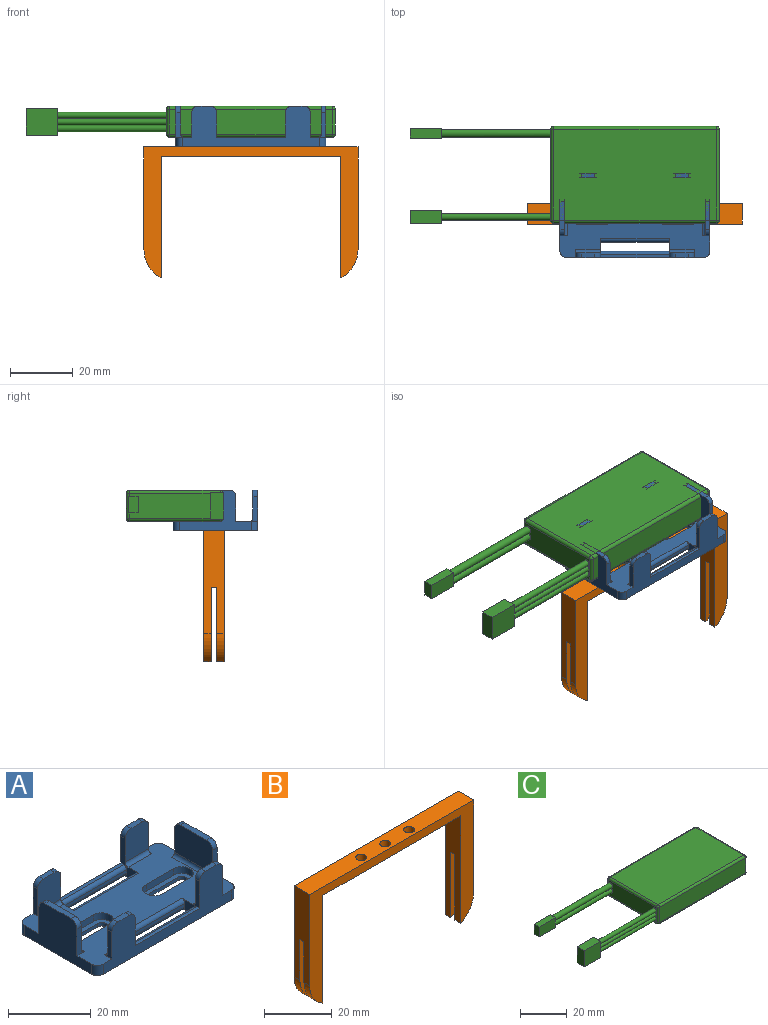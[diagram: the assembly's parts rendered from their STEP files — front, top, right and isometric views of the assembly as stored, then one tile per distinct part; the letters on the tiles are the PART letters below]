
ASSEMBLY  parts=3 mates=2
PART A: 88 faces, bbox 48x27x13 mm
  f0: plane 15x5.6mm, normal (0,0,1), area 42mm2, adj f66,f67,f68,f69,f74,f75,f76,f77
  f1: plane 48x27mm, normal (0,0,-1), area 1002mm2, adj f7,f8,f14,f15,f45,f47,f50,f52
  f2: plane 48x27mm, normal (0,0,1), area 729mm2, adj f7,f8,f14,f15,f21,f22,f23,f24
  f3: plane 22x1mm, normal (0,0,1), area 22mm2, adj f15,f25,f26,f60
  f4: plane 22x1mm, normal (0,0,1), area 22mm2, adj f14,f31,f32,f57
  f5: plane 9x8mm, normal (0,1,0), area 70.3mm2, adj f10,f29,f31,f33,f38,f86
  f6: plane 9x8mm, normal (0,-1,0), area 70.3mm2, adj f13,f26,f28,f36,f44,f84
  f7: plane 23x13mm, normal (1,0,0), area 197.3mm2, adj f1,f2,f9,f27,f30,f35,f37,f78
  f8: plane 23x13mm, normal (-1,0,0), area 197.3mm2, adj f1,f2,f11,f21,f24,f39,f41,f80
  f9: plane 9x1.5mm, normal (0,0,1), area 13.5mm2, adj f7,f17,f35,f37
  f10: plane 4x1.5mm, normal (0,0,1), area 6mm2, adj f5,f14,f33,f38
  f11: plane 9x1.5mm, normal (0,0,1), area 13.5mm2, adj f8,f19,f39,f41
  f12: plane 4x1.5mm, normal (0,0,1), area 6mm2, adj f15,f18,f42,f43
  f13: plane 4x1.5mm, normal (0,0,1), area 6mm2, adj f6,f15,f36,f44
  f14: plane 44x13mm, normal (0,-1,0), area 288.6mm2, adj f1,f2,f4,f10,f20,f23,f29,f31
  f15: plane 44x13mm, normal (0,1,0), area 288.6mm2, adj f1,f2,f3,f12,f13,f22,f25,f26
  f16: plane 9x8mm, normal (0,1,0), area 70.3mm2, adj f20,f23,f32,f34,f40,f83
  f17: plane 13x9mm, normal (-1,0,0), area 115.3mm2, adj f9,f27,f30,f35,f37,f85
  f18: plane 9x8mm, normal (0,-1,0), area 70.3mm2, adj f12,f22,f25,f42,f43,f82
  f19: plane 13x9mm, normal (1,0,0), area 115.3mm2, adj f11,f21,f24,f39,f41,f87
  f20: plane 4x1.5mm, normal (0,0,1), area 6mm2, adj f14,f16,f34,f40
  f21: plane 8x2.5mm, normal (0,1,0), area 12.2mm2, adj f2,f8,f19,f41,f87
  f22: plane 8x2.5mm, normal (-1,0,0), area 12.2mm2, adj f2,f15,f18,f42,f82
  f23: plane 8x2.5mm, normal (-1,0,0), area 12.2mm2, adj f2,f14,f16,f40,f83
  f24: plane 8x2.5mm, normal (0,-1,0), area 12.2mm2, adj f2,f8,f19,f39,f87
  f25: plane 8x2.5mm, normal (1,0,0), area 12.2mm2, adj f3,f15,f18,f43,f50,f82
  f26: plane 8x2.5mm, normal (-1,0,0), area 12.2mm2, adj f3,f6,f15,f44,f52,f84
  f27: plane 8x2.5mm, normal (0,1,0), area 12.2mm2, adj f2,f7,f17,f35,f85
  f28: plane 8x2.5mm, normal (1,0,0), area 12.2mm2, adj f2,f6,f15,f36,f84
  f29: plane 8x2.5mm, normal (1,0,0), area 12.2mm2, adj f2,f5,f14,f38,f86
  f30: plane 8x2.5mm, normal (0,-1,0), area 12.2mm2, adj f2,f7,f17,f37,f85
  f31: plane 8x2.5mm, normal (-1,0,0), area 12.2mm2, adj f4,f5,f14,f33,f47,f86
  f32: plane 8x2.5mm, normal (1,0,0), area 12.2mm2, adj f4,f14,f16,f34,f45,f83
  f33: cylinder r=2mm len=2mm, axis (0,-1,0), area 4.7mm2, adj f5,f10,f14,f31
  f34: cylinder r=2mm len=2mm, axis (0,1,0), area 4.7mm2, adj f14,f16,f20,f32
  f35: cylinder r=2mm len=2mm, axis (-1,0,0), area 4.7mm2, adj f7,f9,f17,f27
  f36: cylinder r=2mm len=2mm, axis (0,1,0), area 4.7mm2, adj f6,f13,f15,f28
  f37: cylinder r=2mm len=2mm, axis (1,0,0), area 4.7mm2, adj f7,f9,f17,f30
  f38: cylinder r=2mm len=2mm, axis (0,1,0), area 4.7mm2, adj f5,f10,f14,f29
  f39: cylinder r=2mm len=2mm, axis (1,0,0), area 4.7mm2, adj f8,f11,f19,f24
  f40: cylinder r=2mm len=2mm, axis (0,-1,0), area 4.7mm2, adj f14,f16,f20,f23
  f41: cylinder r=2mm len=2mm, axis (-1,0,0), area 4.7mm2, adj f8,f11,f19,f21
  f42: cylinder r=2mm len=2mm, axis (0,-1,0), area 4.7mm2, adj f12,f15,f18,f22
  f43: cylinder r=2mm len=2mm, axis (0,1,0), area 4.7mm2, adj f12,f15,f18,f25
  f44: cylinder r=2mm len=2mm, axis (0,-1,0), area 4.7mm2, adj f6,f13,f15,f26
  f45: plane 5x3mm, normal (1,0,0), area 9.9mm2, adj f1,f2,f32,f46,f48,f55,f56,f57
  f46: plane 22x1mm, normal (0,1,0), area 22mm2, adj f45,f47,f55,f57
  f47: plane 5x3mm, normal (-1,0,0), area 9.9mm2, adj f1,f2,f31,f46,f48,f55,f56,f57
  f48: plane 22x1mm, normal (0,-1,0), area 22mm2, adj f45,f47,f56,f58
  f49: plane 22x1mm, normal (0,-1,0), area 22mm2, adj f50,f52,f53,f60
  f50: plane 5x3mm, normal (1,0,0), area 9.9mm2, adj f1,f2,f25,f49,f51,f53,f54,f59
  f51: plane 22x1mm, normal (0,1,0), area 22mm2, adj f50,f52,f54,f59
  f52: plane 5x3mm, normal (-1,0,0), area 9.9mm2, adj f1,f2,f26,f49,f51,f53,f54,f59
  f53: cylinder r=1mm len=22mm, axis (-1,0,0), area 34.6mm2, adj f1,f49,f50,f52
  f54: cylinder r=1mm len=22mm, axis (1,0,0), area 34.6mm2, adj f1,f50,f51,f52
  f55: cylinder r=1mm len=22mm, axis (1,0,0), area 34.6mm2, adj f1,f45,f46,f47
  f56: cylinder r=1mm len=22mm, axis (-1,0,0), area 34.6mm2, adj f1,f45,f47,f48
  f57: cylinder r=1mm len=22mm, axis (-1,0,0), area 34.6mm2, adj f4,f45,f46,f47
  f58: cylinder r=1mm len=22mm, axis (1,0,0), area 34.6mm2, adj f2,f45,f47,f48
  f59: cylinder r=1mm len=22mm, axis (-1,0,0), area 34.6mm2, adj f2,f50,f51,f52
  f60: cylinder r=1mm len=22mm, axis (1,0,0), area 34.6mm2, adj f3,f49,f50,f52
  f61: cylinder r=2.8mm len=5.6mm, axis (0,0,1), area 17.6mm2, adj f2,f62,f64,f65
  f62: plane 9.4x2mm, normal (0,1,0), area 18.8mm2, adj f2,f61,f63,f65
  f63: cylinder r=2.8mm len=5.6mm, axis (0,0,1), area 17.6mm2, adj f2,f62,f64,f65
  f64: plane 9.4x2mm, normal (0,-1,0), area 18.8mm2, adj f2,f61,f63,f65
  f65: plane 15x5.6mm, normal (0,0,1), area 42mm2, adj f61,f62,f63,f64,f70,f71,f72,f73
  f66: cylinder r=2.8mm len=5.6mm, axis (0,0,1), area 17.6mm2, adj f0,f2,f67,f69
  f67: plane 9.4x2mm, normal (0,-1,0), area 18.8mm2, adj f0,f2,f66,f68
  f68: cylinder r=2.8mm len=5.6mm, axis (0,0,1), area 17.6mm2, adj f0,f2,f67,f69
  f69: plane 9.4x2mm, normal (0,1,0), area 18.8mm2, adj f0,f2,f66,f68
  f70: cylinder r=1.5mm len=3mm, axis (0,0,1), area 4.7mm2, adj f1,f65,f71,f73
  f71: plane 9.4x1mm, normal (0,1,0), area 9.4mm2, adj f1,f65,f70,f72
  f72: cylinder r=1.5mm len=3mm, axis (0,0,1), area 4.7mm2, adj f1,f65,f71,f73
  f73: plane 9.4x1mm, normal (0,-1,0), area 9.4mm2, adj f1,f65,f70,f72
  f74: cylinder r=1.5mm len=3mm, axis (0,0,1), area 4.7mm2, adj f0,f1,f75,f77
  f75: plane 9.4x1mm, normal (0,-1,0), area 9.4mm2, adj f0,f1,f74,f76
  f76: cylinder r=1.5mm len=3mm, axis (0,0,1), area 4.7mm2, adj f0,f1,f75,f77
  f77: plane 9.4x1mm, normal (0,1,0), area 9.4mm2, adj f0,f1,f74,f76
  f78: cylinder r=2mm len=3mm, axis (0,0,1), area 9.4mm2, adj f1,f2,f7,f14
  f79: cylinder r=2mm len=3mm, axis (0,0,-1), area 9.4mm2, adj f1,f2,f7,f15
  f80: cylinder r=2mm len=3mm, axis (0,0,1), area 9.4mm2, adj f1,f2,f8,f15
  f81: cylinder r=2mm len=3mm, axis (0,0,-1), area 9.4mm2, adj f1,f2,f8,f14
  f82: cylinder r=1mm len=8mm, axis (1,0,0), area 12.6mm2, adj f2,f18,f22,f25
  f83: cylinder r=1mm len=8mm, axis (-1,0,0), area 12.6mm2, adj f2,f16,f23,f32
  f84: cylinder r=1mm len=8mm, axis (1,0,0), area 12.6mm2, adj f2,f6,f26,f28
  f85: cylinder r=1mm len=13mm, axis (0,-1,0), area 20.4mm2, adj f2,f17,f27,f30
  f86: cylinder r=1mm len=8mm, axis (-1,0,0), area 12.6mm2, adj f2,f5,f29,f31
  f87: cylinder r=1mm len=13mm, axis (0,1,0), area 20.4mm2, adj f2,f19,f21,f24
PART B: 21 faces, bbox 68.5x6.5x41.9 mm
  f0: cylinder r=1.6mm len=3.2mm, axis (0,0,-1), area 30.2mm2, adj f15,f16
  f1: cylinder r=1.6mm len=3.2mm, axis (0,0,-1), area 30.2mm2, adj f15,f16
  f2: plane 38.87x6.5mm, normal (-1,0,0), area 212.4mm2, adj f4,f6,f7,f10,f12,f16,f18,f19
  f3: plane 32.94x6.5mm, normal (1,0,0), area 189mm2, adj f4,f6,f7,f10,f12,f15,f18,f19
  f4: cylinder r=10mm len=8.93mm, axis (0,-1,0), area 26.5mm2, adj f2,f3,f6,f12
  f5: cylinder r=10mm len=8.93mm, axis (0,-1,0), area 26.5mm2, adj f6,f9,f13,f20
  f6: plane 68.5x41.87mm, normal (0,-1,0), area 605.1mm2, adj f2,f3,f4,f5,f9,f15,f16,f20
  f7: cylinder r=10mm len=8.93mm, axis (0,-1,0), area 26.5mm2, adj f2,f3,f18,f19
  f8: cylinder r=10mm len=8.93mm, axis (0,-1,0), area 26.5mm2, adj f9,f14,f19,f20
  f9: plane 38.87x6.5mm, normal (1,0,0), area 212.4mm2, adj f5,f6,f8,f11,f13,f14,f16,f19
  f10: plane 5.5x1.7mm, normal (0,0,-1), area 9.3mm2, adj f2,f3,f12,f18
  f11: plane 5.5x1.7mm, normal (0,0,-1), area 9.4mm2, adj f9,f13,f14,f20
  f12: plane 23.71x5.5mm, normal (0,1,0), area 116.4mm2, adj f2,f3,f4,f10
  f13: plane 23.71x5.5mm, normal (0,1,0), area 116.4mm2, adj f5,f9,f11,f20
  f14: plane 23.71x5.5mm, normal (0,-1,0), area 116.4mm2, adj f8,f9,f11,f20
  f15: plane 68.5x6.5mm, normal (0,0,1), area 421.1mm2, adj f0,f1,f3,f6,f17,f19,f20
  f16: plane 57.5x6.5mm, normal (0,0,-1), area 349.6mm2, adj f0,f1,f2,f6,f9,f17,f19
  f17: cylinder r=1.6mm len=3.2mm, axis (0,0,-1), area 30.2mm2, adj f15,f16
  f18: plane 23.71x5.5mm, normal (0,-1,0), area 116.4mm2, adj f2,f3,f7,f10
  f19: plane 68.5x41.87mm, normal (0,1,0), area 605.1mm2, adj f2,f3,f7,f8,f9,f15,f16,f20
  f20: plane 32.94x6.5mm, normal (-1,0,0), area 189mm2, adj f5,f6,f8,f11,f13,f14,f15,f19
PART C: 46 faces, bbox 99x31.1x10 mm
  f0: plane 2x2mm, normal (1,0,0), area 3.1mm2, adj f1
  f1: cylinder r=1mm len=35mm, axis (1,0,0), area 219.9mm2, adj f0,f2
  f2: plane 8.51x4.28mm, normal (1,0,0), area 26.9mm2, adj f1,f3,f4,f5,f6,f7,f8
  f3: cylinder r=1mm len=35mm, axis (1,0,0), area 219.9mm2, adj f2,f9
  f4: cylinder r=1mm len=35mm, axis (1,0,0), area 219.9mm2, adj f2,f10
  f5: plane 10x8.51mm, normal (0,1,0), area 85.1mm2, adj f2,f6,f8,f11
  f6: plane 10x4.28mm, normal (0,0,1), area 42.7mm2, adj f2,f5,f7,f11
  f7: plane 10x8.51mm, normal (0,-1,0), area 85.1mm2, adj f2,f6,f8,f11
  f8: plane 10x4.28mm, normal (0,0,-1), area 42.7mm2, adj f2,f5,f7,f11
  f9: plane 29x8mm, normal (-1,0,0), area 223.9mm2, adj f3,f12,f13,f14,f15,f16
  f10: plane 2x2mm, normal (1,0,0), area 3.1mm2, adj f4
  f11: plane 8.51x4.28mm, normal (-1,0,0), area 36.4mm2, adj f5,f6,f7,f8
  f12: cylinder r=1mm len=8mm, axis (0,0,1), area 12.6mm2, adj f9,f17,f18,f19
  f13: cylinder r=1mm len=29mm, axis (0,1,0), area 45.6mm2, adj f9,f17,f20,f21
  f14: cylinder r=1mm len=8mm, axis (0,0,-1), area 12.6mm2, adj f9,f20,f22,f23
  f15: cylinder r=1mm len=29mm, axis (0,-1,0), area 45.6mm2, adj f9,f19,f22,f24
  f16: cylinder r=1.25mm len=35mm, axis (1,0,0), area 274.9mm2, adj f9,f25
  f17: sphere r=1mm, area 1.6mm2, adj f12,f13,f26
  f18: plane 52x8mm, normal (0,1,0), area 416mm2, adj f12,f26,f27,f28
  f19: sphere r=1mm, area 1.6mm2, adj f12,f15,f28
  f20: sphere r=1mm, area 1.6mm2, adj f13,f14,f29
  f21: plane 52x29mm, normal (0,0,1), area 1508mm2, adj f13,f26,f29,f30
  f22: sphere r=1mm, area 1.6mm2, adj f14,f15,f31
  f23: plane 52x8mm, normal (0,-1,0), area 416mm2, adj f14,f29,f31,f32
  f24: plane 52x29mm, normal (0,0,-1), area 1508mm2, adj f15,f28,f31,f33
  f25: plane 5.24x3.04mm, normal (1,0,0), area 6.1mm2, adj f16,f34,f35,f36,f37,f38
  f26: cylinder r=1mm len=52mm, axis (1,0,0), area 81.7mm2, adj f17,f18,f21,f39
  f27: cylinder r=1mm len=8mm, axis (0,0,-1), area 12.6mm2, adj f18,f39,f40,f41
  f28: cylinder r=1mm len=52mm, axis (-1,0,0), area 81.7mm2, adj f18,f19,f24,f41
  f29: cylinder r=1mm len=52mm, axis (-1,0,0), area 81.7mm2, adj f20,f21,f23,f42
  f30: cylinder r=1mm len=29mm, axis (0,-1,0), area 45.6mm2, adj f21,f39,f40,f42
  f31: cylinder r=1mm len=52mm, axis (1,0,0), area 81.7mm2, adj f22,f23,f24,f43
  f32: cylinder r=1mm len=8mm, axis (0,0,1), area 12.6mm2, adj f23,f40,f42,f43
  f33: cylinder r=1mm len=29mm, axis (0,1,0), area 45.6mm2, adj f24,f40,f41,f43
  f34: cylinder r=1.25mm len=35mm, axis (1,0,0), area 274.9mm2, adj f25,f44
  f35: plane 10x5.24mm, normal (0,1,0), area 52.4mm2, adj f25,f36,f38,f45
  f36: plane 10x3.04mm, normal (0,0,1), area 30.4mm2, adj f25,f35,f37,f45
  f37: plane 10x5.24mm, normal (0,-1,0), area 52.4mm2, adj f25,f36,f38,f45
  f38: plane 10x3.04mm, normal (0,0,-1), area 30.4mm2, adj f25,f35,f37,f45
  f39: sphere r=1mm, area 1.6mm2, adj f26,f27,f30
  f40: plane 29x8mm, normal (1,0,0), area 232mm2, adj f27,f30,f32,f33
  f41: sphere r=1mm, area 1.6mm2, adj f27,f28,f33
  f42: sphere r=1mm, area 1.6mm2, adj f29,f30,f32
  f43: sphere r=1mm, area 1.6mm2, adj f31,f32,f33
  f44: plane 2.5x2.5mm, normal (1,0,0), area 4.9mm2, adj f34
  f45: plane 5.24x3.04mm, normal (-1,0,0), area 15.9mm2, adj f35,f36,f37,f38
PLACE A t=(10.23,66.36,18.3)mm
PLACE B t=(10.23,67.72,-55.07)mm
PLACE C t=(10.23,79.36,20.3)mm
MATE fastened A.f3 <-> C.f24  axis (0,0,1) through (10.23,79.36,20.3)mm
MATE fastened B.f17 <-> A.f1  axis (0,0,-1) through (10.23,66.36,17.3)mm
